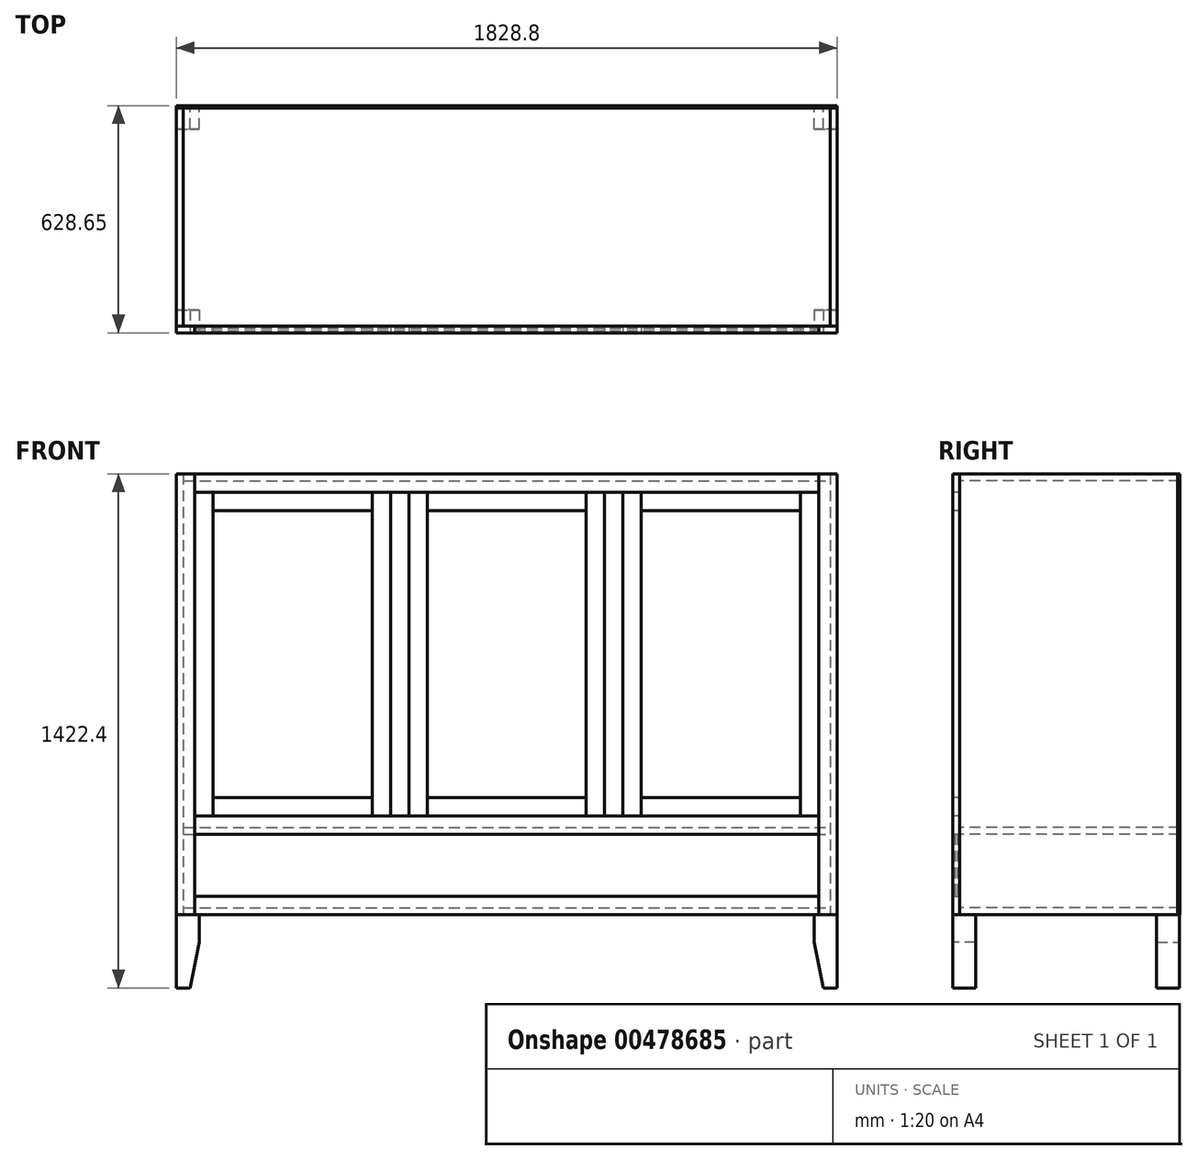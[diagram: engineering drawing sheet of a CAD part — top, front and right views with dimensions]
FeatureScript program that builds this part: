
annotation { "Feature Type Name" : "Feature", "Feature Type Description" : "" }
export const myFeature = defineFeature(function(context is Context, id is Id, definition is map)
    precondition{}
    {
        {
            var Q0;
            Q0=qCreatedBy(makeId("Right.planeOp"),FACE);
            var sketch = newSketch(context, id + "F0", { "sketchPlane" : qUnion([Q0])});
            skLineSegment(sketch, "E0.bottom", {"start": v(-30.46, 1128.18) * mm, "end": v(579.14, 1128.18) * mm});
            skLineSegment(sketch, "E0.top", {"start": v(-30.46, -91.02) * mm, "end": v(579.14, -91.02) * mm});
            skLineSegment(sketch, "E0.left", {"start": v(-30.46, 1128.18) * mm, "end": v(-30.46, -91.02) * mm});
            skLineSegment(sketch, "E0.right", {"start": v(579.14, 1128.18) * mm, "end": v(579.14, -91.02) * mm});
            skSolve(sketch);
        }
        {
            var Q0;
            Q0 = qSketchRegion(id + "F0", true);
            extrude(context, id + "F1", {"entities" : qUnion([Q0]), "depth" : 19.05 * mm});
        }
        {
            var Q0;
            Q0=makeQuery(id+"F1.opExtrude","CAP_FACE",FACE,{"disambiguationData":[OSD([sQuery(id+"F0.wireOp",EDGE,"E0.bottom"),sQuery(id+"F0.wireOp",EDGE,"E0.top"),sQuery(id+"F0.wireOp",EDGE,"E0.left"),sQuery(id+"F0.wireOp",EDGE,"E0.right")])],"isStart":false});
            cPlane(context, id + "F2", {"entities" : qUnion([Q0]), "cplaneType" : CPlaneType.OFFSET, "offset" : 914.4 * mm, "oppositeDirection" : true, "width" : 152.4 * mm, "height" : 152.4 * mm});
        }
        {
            var Q0;
            Q0=makeQuery(id+"F1.opExtrude","SWEPT_BODY",BODY,{"disambiguationData":[OSD([sQuery(id+"F0.wireOp",EDGE,"E0.bottom"),sQuery(id+"F0.wireOp",EDGE,"E0.top"),sQuery(id+"F0.wireOp",EDGE,"E0.left"),sQuery(id+"F0.wireOp",EDGE,"E0.right")])]});
            var Q1;
            Q1=qCreatedBy(id+"F2.planeOp",FACE);
            mirror(context, id + "F3", {"entities" : qUnion([Q0]), "mirrorPlane" : qUnion([Q1])});
        }
        {
            var Q0;
            Q0=makeQuery(id+"F1.opExtrude","SWEPT_FACE",FACE,{"disambiguationData":[OSD([sQuery(id+"F0.wireOp",EDGE,"E0.left")])]});
            var sketch = newSketch(context, id + "F4", { "sketchPlane" : qUnion([Q0])});
            skLineSegment(sketch, "E1.bottom", {"start": v(-1790.7, 1128.18) * mm, "end": v(0, 1128.18) * mm});
            skLineSegment(sketch, "E1.top", {"start": v(-1790.7, 1109.13) * mm, "end": v(0, 1109.13) * mm});
            skLineSegment(sketch, "E1.left", {"start": v(-1790.7, 1128.18) * mm, "end": v(-1790.7, 1109.13) * mm});
            skLineSegment(sketch, "E1.right", {"start": v(0, 1128.18) * mm, "end": v(0, 1109.13) * mm});
            skSolve(sketch);
        }
        {
            var Q0;
            Q0 = qSketchRegion(id + "F4", true);
            extrude(context, id + "F5", {"entities" : qUnion([Q0]), "oppositeDirection" : true, "depth" : 609.6 * mm});
        }
        {
            var Q0;
            Q0=makeQuery(id+"F1.opExtrude","SWEPT_FACE",FACE,{"disambiguationData":[OSD([sQuery(id+"F0.wireOp",EDGE,"E0.left")])]});
            var sketch = newSketch(context, id + "F6", { "sketchPlane" : qUnion([Q0])});
            skLineSegment(sketch, "E2.bottom", {"start": v(-1790.7, -71.97) * mm, "end": v(0, -71.97) * mm});
            skLineSegment(sketch, "E2.top", {"start": v(-1790.7, -91.02) * mm, "end": v(0, -91.02) * mm});
            skLineSegment(sketch, "E2.left", {"start": v(-1790.7, -71.97) * mm, "end": v(-1790.7, -91.02) * mm});
            skLineSegment(sketch, "E2.right", {"start": v(0, -71.97) * mm, "end": v(0, -91.02) * mm});
            skSolve(sketch);
        }
        {
            var Q0;
            Q0 = qSketchRegion(id + "F6", true);
            extrude(context, id + "F7", {"entities" : qUnion([Q0]), "oppositeDirection" : true, "depth" : 609.6 * mm});
        }
        {
            var Q0;
            Q0=makeQuery(id+"F1.opExtrude","SWEPT_FACE",FACE,{"disambiguationData":[OSD([sQuery(id+"F0.wireOp",EDGE,"E0.left")])]});
            var sketch = newSketch(context, id + "F8", { "sketchPlane" : qUnion([Q0])});
            skLineSegment(sketch, "E3.bottom", {"start": v(-1790.7, 150.28) * mm, "end": v(0, 150.28) * mm});
            skLineSegment(sketch, "E3.top", {"start": v(-1790.7, 131.23) * mm, "end": v(0, 131.23) * mm});
            skLineSegment(sketch, "E3.left", {"start": v(-1790.7, 150.28) * mm, "end": v(-1790.7, 131.23) * mm});
            skLineSegment(sketch, "E3.right", {"start": v(0, 150.28) * mm, "end": v(0, 131.23) * mm});
            skSolve(sketch);
        }
        {
            var Q0;
            Q0 = qSketchRegion(id + "F8", true);
            extrude(context, id + "F9", {"entities" : qUnion([Q0]), "oppositeDirection" : true, "depth" : 609.6 * mm});
        }
        {
            var Q0;
            Q0=makeQuery(id+"F1.opExtrude","SWEPT_FACE",FACE,{"disambiguationData":[OSD([sQuery(id+"F0.wireOp",EDGE,"E0.left")])]});
            var sketch = newSketch(context, id + "F10", { "sketchPlane" : qUnion([Q0])});
            skLineSegment(sketch, "E4.bottom", {"start": v(-31.75, 1128.18) * mm, "end": v(19.05, 1128.18) * mm});
            skLineSegment(sketch, "E4.top", {"start": v(-31.75, -91.02) * mm, "end": v(19.05, -91.02) * mm});
            skLineSegment(sketch, "E4.left", {"start": v(-31.75, 1128.18) * mm, "end": v(-31.75, -91.02) * mm});
            skLineSegment(sketch, "E4.right", {"start": v(19.05, 1128.18) * mm, "end": v(19.05, -91.02) * mm});
            skSolve(sketch);
        }
        {
            var Q0;
            Q0 = qSketchRegion(id + "F10", true);
            extrude(context, id + "F11", {"entities" : qUnion([Q0]), "depth" : 19.05 * mm});
        }
        {
            var Q0;
            Q0=makeQuery(id+"F11.opExtrude","SWEPT_BODY",BODY,{"disambiguationData":[OSD([sQuery(id+"F10.wireOp",EDGE,"E4.bottom"),sQuery(id+"F10.wireOp",EDGE,"E4.top"),sQuery(id+"F10.wireOp",EDGE,"E4.left"),sQuery(id+"F10.wireOp",EDGE,"E4.right")])]});
            var Q1;
            Q1=qCreatedBy(id+"F2.planeOp",FACE);
            mirror(context, id + "F12", {"entities" : qUnion([Q0]), "mirrorPlane" : qUnion([Q1])});
        }
        {
            var Q0;
            Q0=makeQuery(id+"F5.opExtrude","CAP_FACE",FACE,{"disambiguationData":[OSD([sQuery(id+"F4.wireOp",EDGE,"E1.bottom"),sQuery(id+"F4.wireOp",EDGE,"E1.top"),sQuery(id+"F4.wireOp",EDGE,"E1.left"),sQuery(id+"F4.wireOp",EDGE,"E1.right")])],"isStart":true});
            var sketch = newSketch(context, id + "F13", { "sketchPlane" : qUnion([Q0])});
            skLineSegment(sketch, "E5.bottom", {"start": v(-1758.95, 1128.18) * mm, "end": v(-31.75, 1128.18) * mm});
            skLineSegment(sketch, "E5.top", {"start": v(-1758.95, 1077.38) * mm, "end": v(-31.75, 1077.38) * mm});
            skLineSegment(sketch, "E5.left", {"start": v(-1758.95, 1128.18) * mm, "end": v(-1758.95, 1077.38) * mm});
            skLineSegment(sketch, "E5.right", {"start": v(-31.75, 1128.18) * mm, "end": v(-31.75, 1077.38) * mm});
            skSolve(sketch);
        }
        {
            var Q0;
            Q0 = qSketchRegion(id + "F13", true);
            extrude(context, id + "F14", {"entities" : qUnion([Q0]), "depth" : 19.05 * mm});
        }
        {
            var Q0;
            Q0=makeQuery(id+"F9.opExtrude","CAP_FACE",FACE,{"disambiguationData":[OSD([sQuery(id+"F8.wireOp",EDGE,"E3.bottom"),sQuery(id+"F8.wireOp",EDGE,"E3.top"),sQuery(id+"F8.wireOp",EDGE,"E3.left"),sQuery(id+"F8.wireOp",EDGE,"E3.right")])],"isStart":true});
            var sketch = newSketch(context, id + "F15", { "sketchPlane" : qUnion([Q0])});
            skLineSegment(sketch, "E6.bottom", {"start": v(-1758.95, 182.03) * mm, "end": v(-31.75, 182.03) * mm});
            skLineSegment(sketch, "E6.top", {"start": v(-1758.95, 131.23) * mm, "end": v(-31.75, 131.23) * mm});
            skLineSegment(sketch, "E6.left", {"start": v(-1758.95, 182.03) * mm, "end": v(-1758.95, 131.23) * mm});
            skLineSegment(sketch, "E6.right", {"start": v(-31.75, 182.03) * mm, "end": v(-31.75, 131.23) * mm});
            skSolve(sketch);
        }
        {
            var Q0;
            Q0 = qSketchRegion(id + "F15", true);
            extrude(context, id + "F16", {"entities" : qUnion([Q0]), "depth" : 19.05 * mm});
        }
        {
            var Q0;
            Q0=makeQuery(id+"F7.opExtrude","CAP_FACE",FACE,{"disambiguationData":[OSD([sQuery(id+"F6.wireOp",EDGE,"E2.bottom"),sQuery(id+"F6.wireOp",EDGE,"E2.top"),sQuery(id+"F6.wireOp",EDGE,"E2.left"),sQuery(id+"F6.wireOp",EDGE,"E2.right")])],"isStart":true});
            var sketch = newSketch(context, id + "F17", { "sketchPlane" : qUnion([Q0])});
            skLineSegment(sketch, "E7.bottom", {"start": v(-1758.95, -91.02) * mm, "end": v(-31.75, -91.02) * mm});
            skLineSegment(sketch, "E7.top", {"start": v(-1758.95, -40.22) * mm, "end": v(-31.75, -40.22) * mm});
            skLineSegment(sketch, "E7.left", {"start": v(-1758.95, -91.02) * mm, "end": v(-1758.95, -40.22) * mm});
            skLineSegment(sketch, "E7.right", {"start": v(-31.75, -91.02) * mm, "end": v(-31.75, -40.22) * mm});
            skSolve(sketch);
        }
        {
            var Q0;
            Q0 = qSketchRegion(id + "F17", true);
            extrude(context, id + "F18", {"entities" : qUnion([Q0]), "depth" : 19.05 * mm});
        }
        {
            var Q0;
            Q0=makeQuery(id+"F12.opPattern","COPY",FACE,{"derivedFrom":makeQuery(id+"F11.opExtrude","CAP_FACE",FACE,{"disambiguationData":[OSD([sQuery(id+"F10.wireOp",EDGE,"E4.bottom"),sQuery(id+"F10.wireOp",EDGE,"E4.top"),sQuery(id+"F10.wireOp",EDGE,"E4.left"),sQuery(id+"F10.wireOp",EDGE,"E4.right")])],"isStart":false}),"instanceName":"1"});
            cPlane(context, id + "F19", {"entities" : qUnion([Q0]), "cplaneType" : CPlaneType.OFFSET, "offset" : 6.35 * mm, "oppositeDirection" : true, "width" : 152.4 * mm, "height" : 152.4 * mm});
        }
        {
            var Q0;
            Q0=qCreatedBy(id+"F19.planeOp",FACE);
            var sketch = newSketch(context, id + "F20", { "sketchPlane" : qUnion([Q0])});
            skLineSegment(sketch, "E8.bottom", {"start": v(-1758.95, 131.23) * mm, "end": v(-31.75, 131.23) * mm});
            skLineSegment(sketch, "E8.top", {"start": v(-1758.95, -40.22) * mm, "end": v(-31.75, -40.22) * mm});
            skLineSegment(sketch, "E8.left", {"start": v(-1758.95, 131.23) * mm, "end": v(-1758.95, -40.22) * mm});
            skLineSegment(sketch, "E8.right", {"start": v(-31.75, 131.23) * mm, "end": v(-31.75, -40.22) * mm});
            skSolve(sketch);
        }
        {
            var Q0;
            Q0=makeQuery(id+"F14.opExtrude","CAP_FACE",FACE,{"disambiguationData":[OSD([sQuery(id+"F13.wireOp",EDGE,"E5.bottom"),sQuery(id+"F13.wireOp",EDGE,"E5.top"),sQuery(id+"F13.wireOp",EDGE,"E5.left"),sQuery(id+"F13.wireOp",EDGE,"E5.right")])],"isStart":false});
            var sketch = newSketch(context, id + "F21", { "sketchPlane" : qUnion([Q0])});
            skLineSegment(sketch, "E9.bottom", {"start": v(-624.33, 1077.38) * mm, "end": v(-573.53, 1077.38) * mm});
            skLineSegment(sketch, "E9.top", {"start": v(-624.33, 182.03) * mm, "end": v(-573.53, 182.03) * mm});
            skLineSegment(sketch, "E9.left", {"start": v(-624.33, 1077.38) * mm, "end": v(-624.33, 182.03) * mm});
            skLineSegment(sketch, "E9.right", {"start": v(-573.53, 1077.38) * mm, "end": v(-573.53, 182.03) * mm});
            skSolve(sketch);
        }
        {
            var Q0;
            Q0 = qSketchRegion(id + "F21", true);
            extrude(context, id + "F22", {"entities" : qUnion([Q0]), "oppositeDirection" : true, "depth" : 19.05 * mm});
        }
        {
            var Q0;
            Q0=makeQuery(id+"F22.opExtrude","SWEPT_BODY",BODY,{"disambiguationData":[OSD([sQuery(id+"F21.wireOp",EDGE,"E9.bottom"),sQuery(id+"F21.wireOp",EDGE,"E9.top"),sQuery(id+"F21.wireOp",EDGE,"E9.left"),sQuery(id+"F21.wireOp",EDGE,"E9.right")])]});
            var Q1;
            Q1=qCreatedBy(id+"F2.planeOp",FACE);
            mirror(context, id + "F23", {"entities" : qUnion([Q0]), "mirrorPlane" : qUnion([Q1])});
        }
        {
            var Q0;
            Q0 = qSketchRegion(id + "F20", true);
            extrude(context, id + "F24", {"entities" : qUnion([Q0]), "oppositeDirection" : true, "depth" : 6.35 * mm});
        }
        {
            var Q0;
            Q0=makeQuery(id+"F14.opExtrude","CAP_FACE",FACE,{"disambiguationData":[OSD([sQuery(id+"F13.wireOp",EDGE,"E5.bottom"),sQuery(id+"F13.wireOp",EDGE,"E5.top"),sQuery(id+"F13.wireOp",EDGE,"E5.left"),sQuery(id+"F13.wireOp",EDGE,"E5.right")])],"isStart":false});
            var sketch = newSketch(context, id + "F25", { "sketchPlane" : qUnion([Q0])});
            skLineSegment(sketch, "E10.bottom", {"start": v(-82.55, 1077.38) * mm, "end": v(-31.75, 1077.38) * mm});
            skLineSegment(sketch, "E10.top", {"start": v(-82.55, 182.03) * mm, "end": v(-31.75, 182.03) * mm});
            skLineSegment(sketch, "E10.left", {"start": v(-82.55, 1077.38) * mm, "end": v(-82.55, 182.03) * mm});
            skLineSegment(sketch, "E10.right", {"start": v(-31.75, 1077.38) * mm, "end": v(-31.75, 182.03) * mm});
            skSolve(sketch);
        }
        {
            var Q0;
            Q0 = qSketchRegion(id + "F25", true);
            extrude(context, id + "F26", {"entities" : qUnion([Q0]), "oppositeDirection" : true, "depth" : 19.05 * mm});
        }
        {
            var Q0;
            Q0=makeQuery(id+"F26.opExtrude","CAP_FACE",FACE,{"disambiguationData":[OSD([sQuery(id+"F25.wireOp",EDGE,"E10.bottom"),sQuery(id+"F25.wireOp",EDGE,"E10.top"),sQuery(id+"F25.wireOp",EDGE,"E10.left"),sQuery(id+"F25.wireOp",EDGE,"E10.right")])],"isStart":true});
            var sketch = newSketch(context, id + "F27", { "sketchPlane" : qUnion([Q0])});
            skLineSegment(sketch, "E11.bottom", {"start": v(-573.53, 1077.38) * mm, "end": v(-522.73, 1077.38) * mm});
            skLineSegment(sketch, "E11.top", {"start": v(-573.53, 182.03) * mm, "end": v(-522.73, 182.03) * mm});
            skLineSegment(sketch, "E11.left", {"start": v(-573.53, 1077.38) * mm, "end": v(-573.53, 182.03) * mm});
            skLineSegment(sketch, "E11.right", {"start": v(-522.73, 1077.38) * mm, "end": v(-522.73, 182.03) * mm});
            skSolve(sketch);
        }
        {
            var Q0;
            Q0 = qSketchRegion(id + "F27", true);
            extrude(context, id + "F28", {"entities" : qUnion([Q0]), "oppositeDirection" : true, "depth" : 19.05 * mm});
        }
        {
            var Q0;
            Q0=makeQuery(id+"F26.opExtrude","CAP_FACE",FACE,{"disambiguationData":[OSD([sQuery(id+"F25.wireOp",EDGE,"E10.bottom"),sQuery(id+"F25.wireOp",EDGE,"E10.top"),sQuery(id+"F25.wireOp",EDGE,"E10.left"),sQuery(id+"F25.wireOp",EDGE,"E10.right")])],"isStart":true});
            var sketch = newSketch(context, id + "F29", { "sketchPlane" : qUnion([Q0])});
            skLineSegment(sketch, "E12.bottom", {"start": v(-522.73, 1077.38) * mm, "end": v(-82.55, 1077.38) * mm});
            skLineSegment(sketch, "E12.top", {"start": v(-522.73, 1026.58) * mm, "end": v(-82.55, 1026.58) * mm});
            skLineSegment(sketch, "E12.left", {"start": v(-522.73, 1077.38) * mm, "end": v(-522.73, 1026.58) * mm});
            skLineSegment(sketch, "E12.right", {"start": v(-82.55, 1077.38) * mm, "end": v(-82.55, 1026.58) * mm});
            skSolve(sketch);
        }
        {
            var Q0;
            Q0 = qSketchRegion(id + "F29", true);
            extrude(context, id + "F30", {"entities" : qUnion([Q0]), "oppositeDirection" : true, "depth" : 19.05 * mm});
        }
        {
            var Q0;
            Q0=makeQuery(id+"F26.opExtrude","CAP_FACE",FACE,{"disambiguationData":[OSD([sQuery(id+"F25.wireOp",EDGE,"E10.bottom"),sQuery(id+"F25.wireOp",EDGE,"E10.top"),sQuery(id+"F25.wireOp",EDGE,"E10.left"),sQuery(id+"F25.wireOp",EDGE,"E10.right")])],"isStart":true});
            var sketch = newSketch(context, id + "F31", { "sketchPlane" : qUnion([Q0])});
            skLineSegment(sketch, "E13.bottom", {"start": v(-522.73, 232.83) * mm, "end": v(-82.55, 232.83) * mm});
            skLineSegment(sketch, "E13.top", {"start": v(-522.73, 182.03) * mm, "end": v(-82.55, 182.03) * mm});
            skLineSegment(sketch, "E13.left", {"start": v(-522.73, 232.83) * mm, "end": v(-522.73, 182.03) * mm});
            skLineSegment(sketch, "E13.right", {"start": v(-82.55, 232.83) * mm, "end": v(-82.55, 182.03) * mm});
            skSolve(sketch);
        }
        {
            var Q0;
            Q0 = qSketchRegion(id + "F31", true);
            extrude(context, id + "F32", {"entities" : qUnion([Q0]), "oppositeDirection" : true, "depth" : 19.05 * mm});
        }
        {
            var Q0;
            Q0=makeQuery(id+"F28.opExtrude","SWEPT_BODY",BODY,{"disambiguationData":[OSD([sQuery(id+"F27.wireOp",EDGE,"E11.bottom"),sQuery(id+"F27.wireOp",EDGE,"E11.top"),sQuery(id+"F27.wireOp",EDGE,"E11.left"),sQuery(id+"F27.wireOp",EDGE,"E11.right")])]});
            var Q1;
            Q1=makeQuery(id+"F30.opExtrude","SWEPT_BODY",BODY,{"disambiguationData":[OSD([sQuery(id+"F29.wireOp",EDGE,"E12.bottom"),sQuery(id+"F29.wireOp",EDGE,"E12.top"),sQuery(id+"F29.wireOp",EDGE,"E12.left"),sQuery(id+"F29.wireOp",EDGE,"E12.right")])]});
            var Q2;
            Q2=makeQuery(id+"F26.opExtrude","SWEPT_BODY",BODY,{"disambiguationData":[OSD([sQuery(id+"F25.wireOp",EDGE,"E10.bottom"),sQuery(id+"F25.wireOp",EDGE,"E10.top"),sQuery(id+"F25.wireOp",EDGE,"E10.left"),sQuery(id+"F25.wireOp",EDGE,"E10.right")])]});
            var Q3;
            Q3=makeQuery(id+"F32.opExtrude","SWEPT_BODY",BODY,{"disambiguationData":[OSD([sQuery(id+"F31.wireOp",EDGE,"E13.bottom"),sQuery(id+"F31.wireOp",EDGE,"E13.top"),sQuery(id+"F31.wireOp",EDGE,"E13.left"),sQuery(id+"F31.wireOp",EDGE,"E13.right")])]});
            var Q4;
            Q4=qCreatedBy(id+"F2.planeOp",FACE);
            mirror(context, id + "F33", {"entities" : qUnion([Q0, Q1, Q2, Q3]), "mirrorPlane" : qUnion([Q4])});
        }
        {
            var Q0;
            Q0=makeQuery(id+"F22.opExtrude","CAP_FACE",FACE,{"disambiguationData":[OSD([sQuery(id+"F21.wireOp",EDGE,"E9.bottom"),sQuery(id+"F21.wireOp",EDGE,"E9.top"),sQuery(id+"F21.wireOp",EDGE,"E9.left"),sQuery(id+"F21.wireOp",EDGE,"E9.right")])],"isStart":true});
            var sketch = newSketch(context, id + "F34", { "sketchPlane" : qUnion([Q0])});
            skLineSegment(sketch, "E14.bottom", {"start": v(-675.13, 1077.38) * mm, "end": v(-624.33, 1077.38) * mm});
            skLineSegment(sketch, "E14.top", {"start": v(-675.13, 182.03) * mm, "end": v(-624.33, 182.03) * mm});
            skLineSegment(sketch, "E14.left", {"start": v(-675.13, 1077.38) * mm, "end": v(-675.13, 182.03) * mm});
            skLineSegment(sketch, "E14.right", {"start": v(-624.33, 1077.38) * mm, "end": v(-624.33, 182.03) * mm});
            skSolve(sketch);
        }
        {
            var Q0;
            Q0 = qSketchRegion(id + "F34", true);
            extrude(context, id + "F35", {"entities" : qUnion([Q0]), "oppositeDirection" : true, "depth" : 19.05 * mm});
        }
        {
            var Q0;
            Q0=makeQuery(id+"F35.opExtrude","CAP_FACE",FACE,{"disambiguationData":[OSD([sQuery(id+"F34.wireOp",EDGE,"E14.bottom"),sQuery(id+"F34.wireOp",EDGE,"E14.top"),sQuery(id+"F34.wireOp",EDGE,"E14.left"),sQuery(id+"F34.wireOp",EDGE,"E14.right")])],"isStart":true});
            var sketch = newSketch(context, id + "F36", { "sketchPlane" : qUnion([Q0])});
            skLineSegment(sketch, "E15.bottom", {"start": v(-1166.37, 1077.38) * mm, "end": v(-1115.57, 1077.38) * mm});
            skLineSegment(sketch, "E15.top", {"start": v(-1166.37, 182.03) * mm, "end": v(-1115.57, 182.03) * mm});
            skLineSegment(sketch, "E15.left", {"start": v(-1166.37, 1077.38) * mm, "end": v(-1166.37, 182.03) * mm});
            skLineSegment(sketch, "E15.right", {"start": v(-1115.57, 1077.38) * mm, "end": v(-1115.57, 182.03) * mm});
            skSolve(sketch);
        }
        {
            var Q0;
            Q0 = qSketchRegion(id + "F36", true);
            extrude(context, id + "F37", {"entities" : qUnion([Q0]), "oppositeDirection" : true, "depth" : 19.05 * mm});
        }
        {
            var Q0;
            Q0=makeQuery(id+"F35.opExtrude","CAP_FACE",FACE,{"disambiguationData":[OSD([sQuery(id+"F34.wireOp",EDGE,"E14.bottom"),sQuery(id+"F34.wireOp",EDGE,"E14.top"),sQuery(id+"F34.wireOp",EDGE,"E14.left"),sQuery(id+"F34.wireOp",EDGE,"E14.right")])],"isStart":true});
            var sketch = newSketch(context, id + "F38", { "sketchPlane" : qUnion([Q0])});
            skLineSegment(sketch, "E16.bottom", {"start": v(-1115.57, 1077.38) * mm, "end": v(-675.13, 1077.38) * mm});
            skLineSegment(sketch, "E16.top", {"start": v(-1115.57, 1026.58) * mm, "end": v(-675.13, 1026.58) * mm});
            skLineSegment(sketch, "E16.left", {"start": v(-1115.57, 1077.38) * mm, "end": v(-1115.57, 1026.58) * mm});
            skLineSegment(sketch, "E16.right", {"start": v(-675.13, 1077.38) * mm, "end": v(-675.13, 1026.58) * mm});
            skSolve(sketch);
        }
        {
            var Q0;
            Q0 = qSketchRegion(id + "F38", true);
            extrude(context, id + "F39", {"entities" : qUnion([Q0]), "oppositeDirection" : true, "depth" : 19.05 * mm});
        }
        {
            var Q0;
            Q0=makeQuery(id+"F35.opExtrude","CAP_FACE",FACE,{"disambiguationData":[OSD([sQuery(id+"F34.wireOp",EDGE,"E14.bottom"),sQuery(id+"F34.wireOp",EDGE,"E14.top"),sQuery(id+"F34.wireOp",EDGE,"E14.left"),sQuery(id+"F34.wireOp",EDGE,"E14.right")])],"isStart":true});
            var sketch = newSketch(context, id + "F40", { "sketchPlane" : qUnion([Q0])});
            skLineSegment(sketch, "E17.bottom", {"start": v(-1115.57, 232.83) * mm, "end": v(-675.13, 232.83) * mm});
            skLineSegment(sketch, "E17.top", {"start": v(-1115.57, 182.03) * mm, "end": v(-675.13, 182.03) * mm});
            skLineSegment(sketch, "E17.left", {"start": v(-1115.57, 232.83) * mm, "end": v(-1115.57, 182.03) * mm});
            skLineSegment(sketch, "E17.right", {"start": v(-675.13, 232.83) * mm, "end": v(-675.13, 182.03) * mm});
            skSolve(sketch);
        }
        {
            var Q0;
            Q0 = qSketchRegion(id + "F40", true);
            extrude(context, id + "F41", {"entities" : qUnion([Q0]), "oppositeDirection" : true, "depth" : 19.05 * mm});
        }
        {
            var Q0;
            Q0=makeQuery(id+"F5.opExtrude","CAP_FACE",FACE,{"disambiguationData":[OSD([sQuery(id+"F4.wireOp",EDGE,"E1.bottom"),sQuery(id+"F4.wireOp",EDGE,"E1.top"),sQuery(id+"F4.wireOp",EDGE,"E1.left"),sQuery(id+"F4.wireOp",EDGE,"E1.right")])],"isStart":false});
            var sketch = newSketch(context, id + "F42", { "sketchPlane" : qUnion([Q0])});
            skLineSegment(sketch, "E18.bottom", {"start": v(-19.05, 1128.18) * mm, "end": v(1809.75, 1128.18) * mm});
            skLineSegment(sketch, "E18.top", {"start": v(-19.05, -91.02) * mm, "end": v(1809.75, -91.02) * mm});
            skLineSegment(sketch, "E18.left", {"start": v(-19.05, 1128.18) * mm, "end": v(-19.05, -91.02) * mm});
            skLineSegment(sketch, "E18.right", {"start": v(1809.75, 1128.18) * mm, "end": v(1809.75, -91.02) * mm});
            skSolve(sketch);
        }
        {
            var Q0;
            Q0 = qSketchRegion(id + "F42", true);
            extrude(context, id + "F43", {"entities" : qUnion([Q0]), "oppositeDirection" : true, "depth" : 6.35 * mm});
        }
        {
            var Q0;
            Q0=makeQuery(id+"F11.opExtrude","CAP_FACE",FACE,{"disambiguationData":[OSD([sQuery(id+"F10.wireOp",EDGE,"E4.bottom"),sQuery(id+"F10.wireOp",EDGE,"E4.top"),sQuery(id+"F10.wireOp",EDGE,"E4.left"),sQuery(id+"F10.wireOp",EDGE,"E4.right")])],"isStart":false});
            var sketch = newSketch(context, id + "F44", { "sketchPlane" : qUnion([Q0])});
            skLineSegment(sketch, "E19", {"start": v(19.05, -91.02) * mm, "end": v(19.05, -294.22) * mm});
            skLineSegment(sketch, "E20", {"start": v(19.05, -294.22) * mm, "end": v(-19.05, -294.22) * mm});
            skLineSegment(sketch, "E21", {"start": v(-19.05, -294.22) * mm, "end": v(-44.45, -167.22) * mm});
            skLineSegment(sketch, "E22", {"start": v(-44.45, -167.22) * mm, "end": v(-44.45, -91.02) * mm});
            skLineSegment(sketch, "E23", {"start": v(-44.45, -91.02) * mm, "end": v(19.05, -91.02) * mm});
            skSolve(sketch);
        }
        {
            var Q0;
            Q0 = qSketchRegion(id + "F44", true);
            extrude(context, id + "F45", {"entities" : qUnion([Q0]), "oppositeDirection" : true, "depth" : 63.5 * mm});
        }
        {
            var Q0;
            Q0=makeQuery(id+"F45.opExtrude","SWEPT_BODY",BODY,{"disambiguationData":[OSD([sQuery(id+"F44.wireOp",EDGE,"E19"),sQuery(id+"F44.wireOp",EDGE,"E20"),sQuery(id+"F44.wireOp",EDGE,"E21"),sQuery(id+"F44.wireOp",EDGE,"E22"),sQuery(id+"F44.wireOp",EDGE,"E23")])]});
            var Q1;
            Q1=qCreatedBy(id+"F2.planeOp",FACE);
            mirror(context, id + "F46", {"entities" : qUnion([Q0]), "mirrorPlane" : qUnion([Q1])});
        }
        {
            var Q0;
            Q0=makeQuery(id+"F5.opExtrude","CAP_FACE",FACE,{"disambiguationData":[OSD([sQuery(id+"F4.wireOp",EDGE,"E1.bottom"),sQuery(id+"F4.wireOp",EDGE,"E1.top"),sQuery(id+"F4.wireOp",EDGE,"E1.left"),sQuery(id+"F4.wireOp",EDGE,"E1.right")])],"isStart":false});
            cPlane(context, id + "F47", {"entities" : qUnion([Q0]), "cplaneType" : CPlaneType.OFFSET, "offset" : 314.96 * mm, "oppositeDirection" : true, "width" : 152.4 * mm, "height" : 152.4 * mm});
        }
        {
            var Q0;
            Q0=makeQuery(id+"F46.opPattern","COPY",BODY,{"derivedFrom":makeQuery(id+"F45.opExtrude","SWEPT_BODY",BODY,{"disambiguationData":[OSD([sQuery(id+"F44.wireOp",EDGE,"E19"),sQuery(id+"F44.wireOp",EDGE,"E20"),sQuery(id+"F44.wireOp",EDGE,"E21"),sQuery(id+"F44.wireOp",EDGE,"E22"),sQuery(id+"F44.wireOp",EDGE,"E23")])]}),"instanceName":"1"});
            var Q1;
            Q1=makeQuery(id+"F45.opExtrude","SWEPT_BODY",BODY,{"disambiguationData":[OSD([sQuery(id+"F44.wireOp",EDGE,"E19"),sQuery(id+"F44.wireOp",EDGE,"E20"),sQuery(id+"F44.wireOp",EDGE,"E21"),sQuery(id+"F44.wireOp",EDGE,"E22"),sQuery(id+"F44.wireOp",EDGE,"E23")])]});
            var Q2;
            Q2=qCreatedBy(id+"F47.planeOp",FACE);
            mirror(context, id + "F48", {"entities" : qUnion([Q0, Q1]), "mirrorPlane" : qUnion([Q2])});
        }
    });
